# Revit family: РОСМА_КлапанЭлектромагнитный_СК
name_source: partatom
category: Арматура трубопроводов
revit_build: Autodesk Revit 2018 (Build: 20180423_1000(x64)
units: mm (PartAtom-declared; Revit-internal decimal feet)

## family parameters
Всегда вертикально = Да
На основе рабочей плоскости = Нет
Общий = Нет
При загрузке вырезать с полостями = Да
Размер круглого соединителя = Использовать диаметр
Тип детали = Вставляется

## types (2) — shared parameters
ADSK_Единица измерения = шт.
ADSK_Количество = 1
Table1 = размеры_соленоид прямого действия
Table2 = спец_ск
URL = https://rosma.spb.ru
Изготовитель = ЗАО "РОСМА"
Климатическое исполнение = Группа В3 по ГОСТ Р 52931; климатическое исполнение УХЛ категории 3.1 по ГОСТ 15150
Материал корпуса 2 = _Черный пластик
Материал корпуса 3 = _Стекло
Мембрана = Бутадиен-нитрильный каучук (NBR); фторкаучук (Витон)
Надежность = 500000
Номинальное напряжение = ~220 В, -24В
Описание = Тип СК. Клапаны двухпозиционные двухходовые электромагнитные предназначены для автоматического управления (открытие, закрытие) потоками воды, масла, сжатого воздуха, нейтральных газов и прочих сред: агрессивных (для корпуса из нержавеющей стали) и неагрессивных к медным сплавам (для корпуса из медного сплава) и каучукам. Прямого действия.
Раб. давление = Воздух, газ: 0…1,0; Вода: 0…0,7; Масло: 0…0,9
Степень защиты катушки = IP65, DIN-разъем
Температура окр. среды = от -10°С до +80°С
Температура раб. среды с мембраной NBR = от -5°С до +90°С
Температура раб. среды с мембраной витон = от -10°С до +120°С
Техническая документация = ТУ 3712-001-4719015564-2015

## per-type parameters (varying)
| type | Материал корпуса 1 | Тип |
| СК медный сплав | _Медный сплав | 1 |
| СК нержавеющая сталь | _Нержавеющая сталь | 2 |
